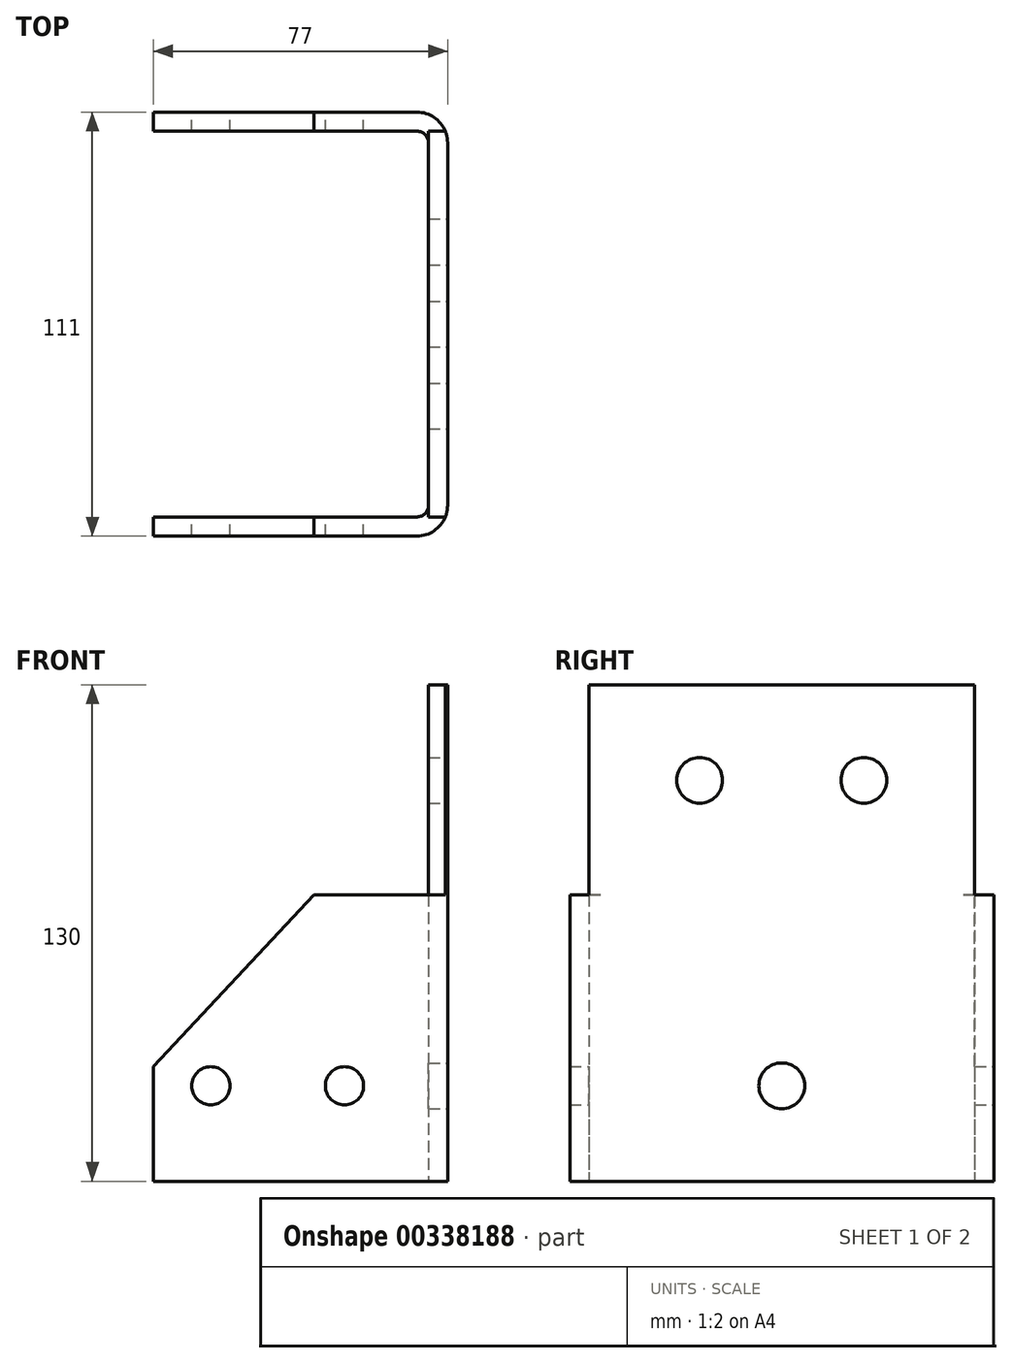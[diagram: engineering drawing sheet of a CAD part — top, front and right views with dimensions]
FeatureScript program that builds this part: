
annotation { "Feature Type Name" : "Feature", "Feature Type Description" : "" }
export const myFeature = defineFeature(function(context is Context, id is Id, definition is map)
    precondition{}
    {
        {
            var Q0;
            Q0=qCreatedBy(makeId("Top.planeOp"),FACE);
            var sketch = newSketch(context, id + "F0", { "sketchPlane" : qUnion([Q0])});
            skLineSegment(sketch, "E0", {"start": v(0, 0) * mm, "end": v(69, 0) * mm});
            skLineSegment(sketch, "E1", {"start": v(77, -8) * mm, "end": v(77, -103) * mm});
            skLineSegment(sketch, "E2", {"start": v(69, -111) * mm, "end": v(0, -111) * mm});
            skLineSegment(sketch, "E3", {"start": v(0, 0) * mm, "end": v(0, -5) * mm});
            skLineSegment(sketch, "E4", {"start": v(0, -5) * mm, "end": v(69, -5) * mm});
            skLineSegment(sketch, "E5", {"start": v(72, -8) * mm, "end": v(72, -103) * mm});
            skLineSegment(sketch, "E6", {"start": v(69, -106) * mm, "end": v(0, -106) * mm});
            skLineSegment(sketch, "E7", {"start": v(0, -106) * mm, "end": v(0, -111) * mm});
            skPoint(sketch, "E8.visualSharp", {"position": v(72, -5) * mm});
            skArc(sketch, "E8.filletArc", {"start": v(72, -8) * mm, "mid": v(71.12, -5.88) * mm, "end": v(69, -5) * mm});
            skPoint(sketch, "E9.visualSharp", {"position": v(72, -106) * mm});
            skArc(sketch, "E9.filletArc", {"start": v(69, -106) * mm, "mid": v(71.12, -105.12) * mm, "end": v(72, -103) * mm});
            skPoint(sketch, "E10.visualSharp", {"position": v(77, 0) * mm});
            skArc(sketch, "E10.filletArc", {"start": v(77, -8) * mm, "mid": v(74.66, -2.34) * mm, "end": v(69, 0) * mm});
            skPoint(sketch, "E11.visualSharp", {"position": v(77, -111) * mm});
            skArc(sketch, "E11.filletArc", {"start": v(69, -111) * mm, "mid": v(74.66, -108.66) * mm, "end": v(77, -103) * mm});
            skSolve(sketch);
        }
        {
            var Q0;
            Q0 = qSketchRegion(id + "F0", true);
            extrude(context, id + "F1", {"entities" : qUnion([Q0]), "depth" : 130 * mm});
        }
        {
            var Q0;
            Q0=makeQuery(id+"F1.opExtrude","SWEPT_FACE",FACE,{"disambiguationData":[OSD([sQuery(id+"F0.wireOp",EDGE,"E0")])]});
            cPlane(context, id + "F2", {"entities" : qUnion([Q0]), "cplaneType" : CPlaneType.OFFSET, "offset" : 0 * mm, "width" : 150 * mm, "height" : 150 * mm});
        }
        {
            var Q0;
            Q0=qCreatedBy(id+"F2.planeOp",FACE);
            var sketch = newSketch(context, id + "F3", { "sketchPlane" : qUnion([Q0])});
            skLineSegment(sketch, "E12", {"start": v(0, 130) * mm, "end": v(-72, 130) * mm});
            skLineSegment(sketch, "E13", {"start": v(-72, 130) * mm, "end": v(-72, 75) * mm});
            skLineSegment(sketch, "E14", {"start": v(-72, 75) * mm, "end": v(-42, 75) * mm});
            skLineSegment(sketch, "E15", {"start": v(-42, 75) * mm, "end": v(0, 75) * mm});
            skLineSegment(sketch, "E16", {"start": v(0, 75) * mm, "end": v(0, 130) * mm});
            skSolve(sketch);
        }
        {
            var Q0;
            Q0 = qSketchRegion(id + "F3", true);
            extrude(context, id + "F4", {"entities" : qUnion([Q0]), "operationType" : NewBodyOperationType.REMOVE, "oppositeDirection" : true, "depth" : 121 * mm});
        }
        {
            var Q0;
            Q0=qCreatedBy(id+"F2.planeOp",FACE);
            var sketch = newSketch(context, id + "F5", { "sketchPlane" : qUnion([Q0])});
            skLineSegment(sketch, "E17", {"start": v(0, 75) * mm, "end": v(-42, 75) * mm});
            skLineSegment(sketch, "E18", {"start": v(0, 30) * mm, "end": v(-42, 75) * mm});
            skLineSegment(sketch, "E19", {"start": v(0, 75) * mm, "end": v(0, 30) * mm});
            skSolve(sketch);
        }
        {
            var Q0;
            Q0 = qSketchRegion(id + "F5", true);
            extrude(context, id + "F6", {"entities" : qUnion([Q0]), "operationType" : NewBodyOperationType.REMOVE, "oppositeDirection" : true, "depth" : 116 * mm});
        }
        {
            var Q0;
            Q0=makeQuery(id+"F1.opExtrude","SWEPT_FACE",FACE,{"disambiguationData":[OSD([sQuery(id+"F0.wireOp",EDGE,"E1")])]});
            cPlane(context, id + "F7", {"entities" : qUnion([Q0]), "cplaneType" : CPlaneType.OFFSET, "offset" : 0 * mm, "width" : 150 * mm, "height" : 150 * mm});
        }
        {
            var Q0;
            Q0=qCreatedBy(id+"F7.planeOp",FACE);
            var sketch = newSketch(context, id + "F8", { "sketchPlane" : qUnion([Q0])});
            skLineSegment(sketch, "E20", {"start": v(0, 0) * mm, "end": v(0, 75) * mm});
            skLineSegment(sketch, "E21", {"start": v(0, 75) * mm, "end": v(-5, 75) * mm});
            skLineSegment(sketch, "E22", {"start": v(-5, 75) * mm, "end": v(-5, 130) * mm});
            skLineSegment(sketch, "E23", {"start": v(-5, 130) * mm, "end": v(0, 130) * mm});
            skLineSegment(sketch, "E24", {"start": v(0, 130) * mm, "end": v(0, 75) * mm});
            skSolve(sketch);
        }
        {
            var Q0;
            Q0 = qSketchRegion(id + "F8", true);
            extrude(context, id + "F9", {"entities" : qUnion([Q0]), "operationType" : NewBodyOperationType.REMOVE, "oppositeDirection" : true, "depth" : 37.8 * mm});
        }
        {
            var Q0;
            Q0=qCreatedBy(id+"F7.planeOp",FACE);
            var sketch = newSketch(context, id + "F10", { "sketchPlane" : qUnion([Q0])});
            skLineSegment(sketch, "E25", {"start": v(0, 0) * mm, "end": v(-106, 0) * mm});
            skLineSegment(sketch, "E26", {"start": v(-106, 75) * mm, "end": v(-106, 130) * mm});
            skLineSegment(sketch, "E27", {"start": v(-106, 130) * mm, "end": v(-111, 130) * mm});
            skLineSegment(sketch, "E28", {"start": v(-111, 130) * mm, "end": v(-111, 75) * mm});
            skLineSegment(sketch, "E29", {"start": v(-111, 75) * mm, "end": v(-106, 75) * mm});
            skSolve(sketch);
        }
        {
            var Q0;
            Q0 = qSketchRegion(id + "F10", true);
            extrude(context, id + "F11", {"entities" : qUnion([Q0]), "operationType" : NewBodyOperationType.REMOVE, "oppositeDirection" : true, "depth" : 63 * mm});
        }
        {
            var Q0;
            Q0=qCreatedBy(id+"F2.planeOp",FACE);
            var sketch = newSketch(context, id + "F12", { "sketchPlane" : qUnion([Q0])});
            skCircle(sketch, "E30", {"center": v(-15, 25) * mm, "radius": 5 * mm});
            skCircle(sketch, "E31", {"center": v(-50, 25) * mm, "radius": 5 * mm});
            skSolve(sketch);
        }
        {
            var Q0;
            Q0 = qSketchRegion(id + "F12", true);
            extrude(context, id + "F13", {"entities" : qUnion([Q0]), "operationType" : NewBodyOperationType.REMOVE, "oppositeDirection" : true, "depth" : 135 * mm});
        }
        {
            var Q0;
            Q0=qCreatedBy(id+"F7.planeOp",FACE);
            var sketch = newSketch(context, id + "F14", { "sketchPlane" : qUnion([Q0])});
            skCircle(sketch, "E32", {"center": v(-55.5, 25) * mm, "radius": 6 * mm});
            skCircle(sketch, "E33", {"center": v(-77, 105) * mm, "radius": 6 * mm});
            skCircle(sketch, "E34", {"center": v(-34, 105) * mm, "radius": 6 * mm});
            skSolve(sketch);
        }
        {
            var Q0;
            Q0 = qSketchRegion(id + "F14", true);
            extrude(context, id + "F15", {"entities" : qUnion([Q0]), "operationType" : NewBodyOperationType.REMOVE, "oppositeDirection" : true, "depth" : 25 * mm});
        }
    });
